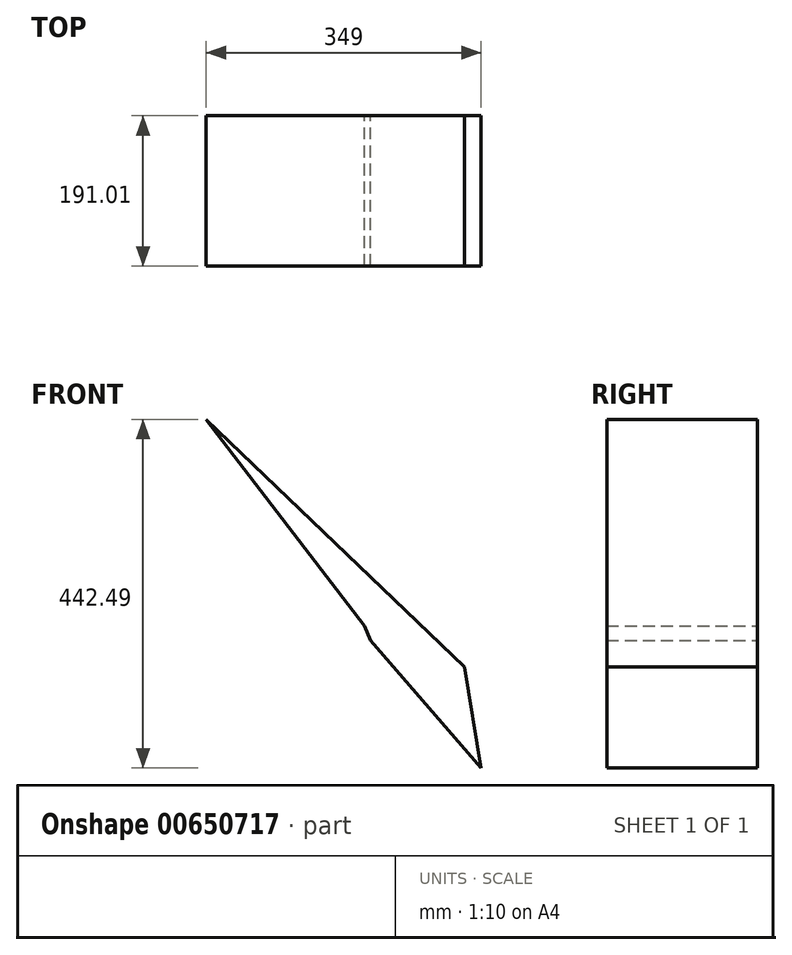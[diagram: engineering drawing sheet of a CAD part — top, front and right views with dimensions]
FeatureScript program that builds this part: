
annotation { "Feature Type Name" : "Feature", "Feature Type Description" : "" }
export const myFeature = defineFeature(function(context is Context, id is Id, definition is map)
    precondition{}
    {
        {
            var Q0;
            Q0=qCreatedBy(makeId("Front.planeOp"),FACE);
            var sketch = newSketch(context, id + "F0", { "sketchPlane" : qUnion([Q0])});
            skLineSegment(sketch, "E0", {"start": v(78.47, -91.83) * mm, "end": v(-61.74, 69.89) * mm});
            skLineSegment(sketch, "E1", {"start": v(-61.74, 69.89) * mm, "end": v(57.52, 36.64) * mm});
            skLineSegment(sketch, "E2", {"start": v(78.47, -91.83) * mm, "end": v(57.52, 36.64) * mm});
            skLineSegment(sketch, "E3", {"start": v(59.03, 36.64) * mm, "end": v(9.21, -76.51) * mm});
            skLineSegment(sketch, "E4", {"start": v(78.47, -91.83) * mm, "end": v(834, -1326.08) * mm});
            skLineSegment(sketch, "E5", {"start": v(-611.66, 809.23) * mm, "end": v(-570.47, 844.94) * mm});
            skLineSegment(sketch, "E6", {"start": v(-570.47, 844.94) * mm, "end": v(-270.53, 350.66) * mm});
            skLineSegment(sketch, "E7", {"start": v(-270.53, 350.66) * mm, "end": v(-69.19, 88.35) * mm});
            skLineSegment(sketch, "E8", {"start": v(-69.19, 88.35) * mm, "end": v(-61.74, 69.89) * mm});
            skLineSegment(sketch, "E9", {"start": v(57.52, 36.64) * mm, "end": v(-270.53, 350.66) * mm});
            skSolve(sketch);
        }
        {
            var Q0;
            Q0 = qSketchRegion(id + "F0", true);
            extrude(context, id + "F1", {"entities" : qUnion([Q0]), "depth" : 25.4 * mm, "offsetDistance" : 25.4 * mm});
        }
        {
            var Q0;
            Q0=makeQuery(id+"F1.opExtrude","CAP_FACE",FACE,{"disambiguationData":[OSD([sQuery(id+"F0.wireOp",EDGE,"E0"),sQuery(id+"F0.wireOp",EDGE,"E2"),sQuery(id+"F0.wireOp",EDGE,"E7"),sQuery(id+"F0.wireOp",EDGE,"E8"),sQuery(id+"F0.wireOp",EDGE,"E9")])],"isStart":true});
            extrude(context, id + "F2", {"entities" : qUnion([Q0]), "operationType" : NewBodyOperationType.ADD, "depth" : 165.6 * mm, "offsetDistance" : 25.4 * mm});
        }
    });
